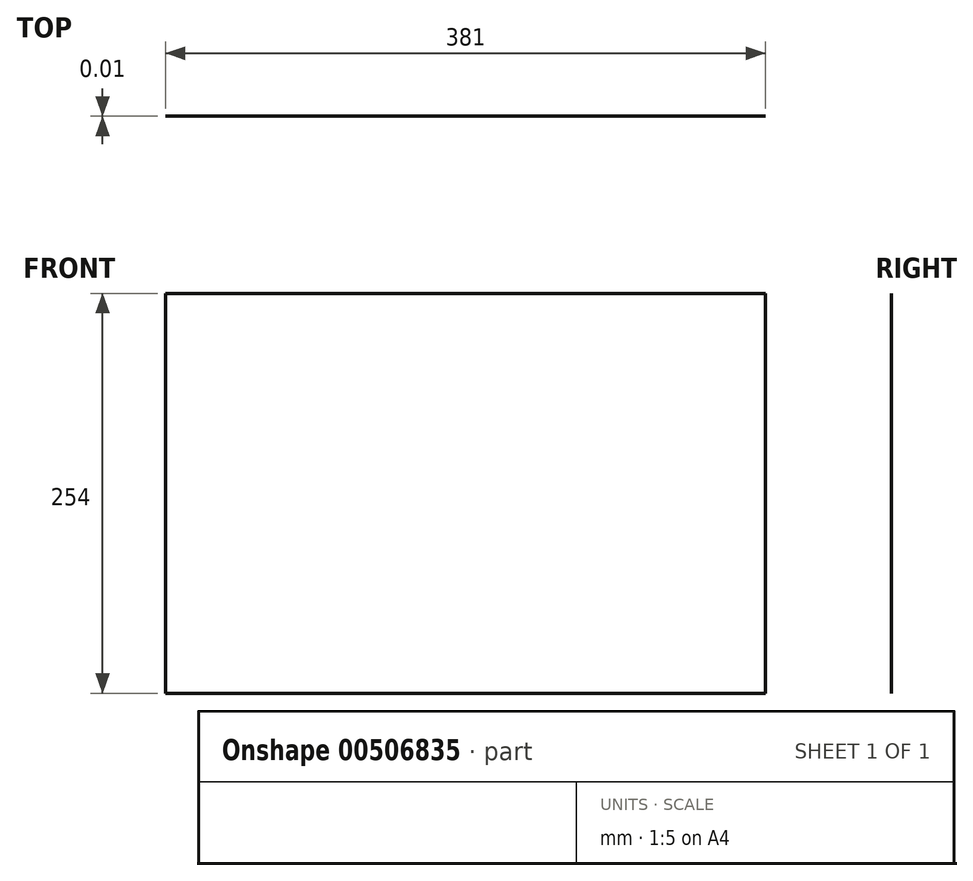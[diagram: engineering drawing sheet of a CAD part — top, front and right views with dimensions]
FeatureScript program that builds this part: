
annotation { "Feature Type Name" : "Feature", "Feature Type Description" : "" }
export const myFeature = defineFeature(function(context is Context, id is Id, definition is map)
    precondition{}
    {
        {
            var Q0;
            Q0=qCreatedBy(makeId("Front.planeOp"),FACE);
            var sketch = newSketch(context, id + "F0", { "sketchPlane" : qUnion([Q0])});
            skLineSegment(sketch, "E0.bottom", {"start": v(-62.1, -31.4) * mm, "end": v(318.9, -31.4) * mm});
            skLineSegment(sketch, "E0.top", {"start": v(-62.1, 222.6) * mm, "end": v(318.9, 222.6) * mm});
            skLineSegment(sketch, "E0.left", {"start": v(-62.1, -31.4) * mm, "end": v(-62.1, 222.6) * mm});
            skLineSegment(sketch, "E0.right", {"start": v(318.9, -31.4) * mm, "end": v(318.9, 222.6) * mm});
            skSolve(sketch);
        }
        {
            var Q0;
            Q0=makeQuery(id+"F0.imprint","IMPRINT",FACE,{"disambiguationData":[TD([[makeQuery(id+"F0.imprint","IMPRINT",EDGE,{"derivedFrom":sQuery(id+"F0.wireOp",EDGE,"E0.bottom")}),1.0]])]});
            extrude(context, id + "F1", {"entities" : qUnion([Q0]), "depth" : 5 / 406.4 * mm, "offsetDistance" : 25.4 * mm});
        }
    });
